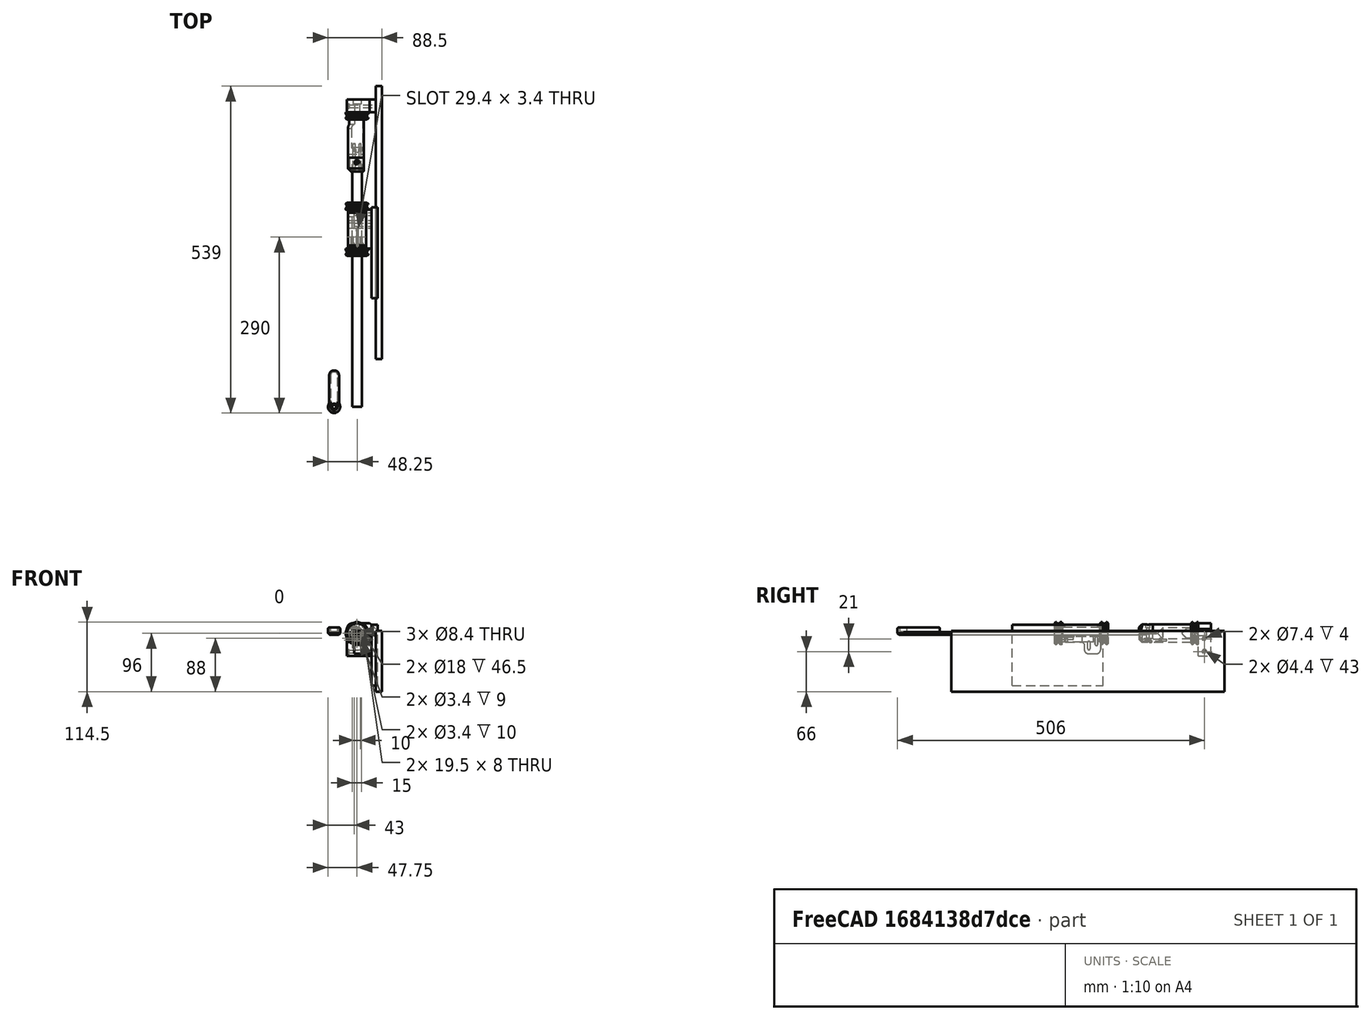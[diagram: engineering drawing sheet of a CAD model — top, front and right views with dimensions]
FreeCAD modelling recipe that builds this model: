
FCSTD DOCUMENT  (FreeCAD 0.16R6703 (Git))
Label: lathe-scale
License: All rights reserved
LicenseURL: http://en.wikipedia.org/wiki/All_rights_reserved
objects: Part::Cylinder×43, Part::Cut×42, Part::Chamfer×35, Part::MultiFuse×35, Part::Box×33, Part::Feature×21, Part::Fillet×11, Part::Mirroring×5, App::DocumentObjectGroup×2, Part::Ellipse×1, Part::Extrusion×1, Part::Fuse×1
note: 228 computed .brp shape members not serialized (recipe doc carries the construction recipe); baked Part::Feature solids carry a one-line shape summary decoded from their .brp

FEATURE [Part::Box] Box  label="scale"
  Height = 4
  Length = 15.5
  Width = 400
FEATURE [Part::Box] Box001  label="slider"
  Height = 15
  Length = 30
  Placement = pos=(-7,263,-2.5) rot=(0,0,1;0rad)
  Width = 60
FEATURE [Part::Ellipse] Ellipse
  Angle0 = 0
  Angle1 = 360
  MajorRadius = 15
  MinorRadius = 10
FEATURE [Part::Feature] Face
  shape: bbox 43.11 x 21.77 x 2e-07 mm, 1 faces, 0 solids (baked)
FEATURE [Part::Extrusion] Extrude
  Base = -> Face
  Dir = (0,0,15)
  Placement = pos=(7.75,390,2) rot=(-1,0,0;1.5708rad)
  Solid = true
  TaperAngle = 15
FEATURE [Part::Cylinder] Cylinder  label="end-cheek"
  Angle = 360
  Height = 3
  Placement = pos=(7.75,486,2) rot=(1,0,0;1.5708rad)
  Radius = 18.5
FEATURE [Part::Cylinder] Cylinder001  label="cable-tie-cyl"
  Angle = 360
  Height = 10
  Placement = pos=(7.75,485,2) rot=(1,0,0;1.5708rad)
  Radius = 16.5
FEATURE [Part::Cylinder] Cylinder002  label="inside-cheek"
  Angle = 360
  Height = 3
  Placement = pos=(7.75,477,2) rot=(1,0,0;1.5708rad)
  Radius = 18.5
FEATURE [Part::Box] Box002  label="lathe-face-1"
  Height = 100
  Length = 10
  Placement = pos=(38.5,79,-94) rot=(0,0,1;0rad)
  Width = 450
FEATURE [Part::Cylinder] Cylinder003
  Angle = 360
  Height = 97
  Placement = pos=(7.75,485,2) rot=(1,0,0;1.5708rad)
  Radius = 15
FEATURE [Part::Chamfer] Chamfer  label="mandrel"
  Base = -> Cylinder003
  Edges = 1 edges r=5: [Edge1]
FEATURE [Part::Box] Box003  label="slot"
  Height = 2
  Length = 35
  Placement = pos=(-10,377,1) rot=(0,0,1;0rad)
  Width = 40
FEATURE [Part::Box] Box004  label="scale-hole"
  Height = 4
  Length = 15.5
  Placement = pos=(0,380,0) rot=(0,0,1;0rad)
  Width = 20
FEATURE [Part::Cylinder] Cylinder004  label="M4"
  Angle = 360
  Height = 36
  Placement = pos=(7.75,403,-15) rot=(0,0,1;0rad)
  Radius = 2.2
FEATURE [Part::Cylinder] Cylinder005  label="M4-head"
  Angle = 360
  Height = 8
  Placement = pos=(7.75,403,11) rot=(0,0,1;0rad)
  Radius = 3.8
FEATURE [Part::Cylinder] Cylinder006
  Angle = 360
  Height = 8
  Placement = pos=(0,0,1) rot=(0,0,1;0rad)
  Radius = 6
FEATURE [Part::Box] Box005  label="Cube"
  Height = 10
  Length = 10
  Placement = pos=(3.7,-5,0) rot=(0,0,1;0rad)
  Width = 10
FEATURE [Part::Feature] Box005001
  Placement = pos=(6.18013,0.704294,0) rot=(0,0,1;1.0472rad)
  shape: bbox 13.66 x 13.66 x 10 mm, 6 faces (baked)
FEATURE [Part::Feature] Box005002
  Placement = pos=(2.48013,5.70429,0) rot=(0,0,1;2.0944rad)
  shape: bbox 13.66 x 13.66 x 10 mm, 6 faces (baked)
FEATURE [Part::Feature] Box005003
  Placement = pos=(-3.7,5,0) rot=(0,0,1;3.14159rad)
  shape: bbox 10 x 10 x 10 mm, 6 faces (baked)
FEATURE [Part::Feature] Box005004
  Placement = pos=(-6.18013,-0.704294,0) rot=(0,0,1;4.18879rad)
  shape: bbox 13.66 x 13.66 x 10 mm, 6 faces (baked)
FEATURE [Part::Feature] Box005005
  Placement = pos=(-2.48013,-5.70429,0) rot=(0,0,-1;1.0472rad)
  shape: bbox 13.66 x 13.66 x 10 mm, 6 faces (baked)
FEATURE [Part::MultiFuse] Fusion
  Shapes = -> [Box005,Box005003,Box005002,Box005004,Box005001,Box005005]
FEATURE [Part::Cut] Cut  label="M4-nut"
  Base = -> Cylinder006
  Placement = pos=(7.75,403,-15) rot=(0,0,1;0rad)
  Tool = -> Fusion
FEATURE [Part::Cylinder] Cylinder007
  Angle = 360
  Height = 70
  Placement = pos=(7.75,485,2) rot=(1,0,0;1.5708rad)
  Radius = 9
FEATURE [Part::Chamfer] Chamfer001  label="hollow"
  Base = -> Cylinder007
  Edges = 1 edges r=8.5: [Edge1]
  Placement = pos=(0,4,0) rot=(0,0,1;0rad)
FEATURE [Part::Box] Box005006  label="gap-expander"
  Height = 30
  Length = 35
  Placement = pos=(19,377,-14) rot=(0,0,1;0rad)
  Width = 140
FEATURE [Part::Cut] Cut001
  Base = -> Chamfer
  Tool = -> Chamfer001
FEATURE [Part::Cut] Cut002
  Base = -> Cut001
  Tool = -> Box005006
FEATURE [Part::Fillet] Fillet
  Base = -> Cut002
  Edges = 1 edges r=4: [Edge4]
FEATURE [Part::Fillet] Fillet001
  Base = -> Fillet
  Edges = 1 edges r=4: [Edge3]
FEATURE [Part::Cut] Cut003
  Base = -> Fillet001
  Tool = -> Box003
FEATURE [Part::Cut] Cut004
  Base = -> Cut003
  Tool = -> Box004
FEATURE [Part::Cut] Cut005
  Base = -> Cut004
  Tool = -> Cut
FEATURE [Part::Cut] Cut006
  Base = -> Cut005
  Tool = -> Cylinder005
FEATURE [Part::Cut] Cut007
  Base = -> Cut006
  Tool = -> Cylinder004
FEATURE [Part::MultiFuse] Fusion001  label="mandrel-no-mount"
  Shapes = -> [Cut007,Cylinder002,Cylinder001,Cylinder]
FEATURE [Part::Box] Box005007  label="bracket-blank"
  Height = 54
  Length = 47.5
  Placement = pos=(-9,486,-35) rot=(0,0,1;0rad)
  Width = 21
FEATURE [Part::Cylinder] Cylinder008
  Angle = 360
  Height = 70
  Placement = pos=(7.75,531,2) rot=(1,0,0;1.5708rad)
  Radius = 4.2
FEATURE [Part::Box] Box005008  label="bracket-blank001"
  Height = 16
  Length = 38
  Placement = pos=(-30,459,-6) rot=(0,0,1;0rad)
  Width = 15
FEATURE [Part::Chamfer] Chamfer002
  Base = -> Box005008
  Edges = 1 edges r=7.5: [Edge10]
FEATURE [Part::Chamfer] Chamfer003  label="nut-access"
  Base = -> Chamfer002
  Edges = 1 edges r=7.5: [Edge8]
FEATURE [Part::Cut] Cut008
  Base = -> Fusion001
  Tool = -> Chamfer003
FEATURE [Part::Chamfer] Chamfer004
  Base = -> Cut008
  Edges = 3 edges r=2: [Edge9,Edge10,Edge11]
FEATURE [Part::Chamfer] Chamfer005
  Base = -> Chamfer004
  Edges = 1 edges r=1.9: [Edge21]
FEATURE [Part::Chamfer] Chamfer006
  Base = -> Chamfer005
  Edges = 1 edges r=1.9: [Edge3]
FEATURE [Part::Cylinder] Cylinder009
  Angle = 360
  Height = 20
  Placement = pos=(7.75,531,2) rot=(1,0,0;1.5708rad)
  Radius = 10
FEATURE [Part::Box] Box005009  label="bracket-blank002"
  Height = 34
  Length = 38
  Placement = pos=(-9,510,8.7) rot=(0,0,1;0rad)
  Width = 22
FEATURE [Part::Feature] Box005009001
  Placement = pos=(5.17737,510,19.8559) rot=(0,1,0;1.0472rad)
  shape: bbox 48.44 x 22 x 49.91 mm, 6 faces (baked)
FEATURE [Part::Feature] Box005009002
  Placement = pos=(21.9274,510,13.1559) rot=(0,1,0;2.0944rad)
  shape: bbox 48.44 x 22 x 49.91 mm, 6 faces (baked)
FEATURE [Part::Feature] Box005009003
  Placement = pos=(24.5,510,-4.7) rot=(0,1,0;3.14159rad)
  shape: bbox 38 x 22 x 34 mm, 6 faces (baked)
FEATURE [Part::Feature] Box005009004
  Placement = pos=(10.3226,510,-15.8559) rot=(0,1,0;4.18879rad)
  shape: bbox 48.44 x 22 x 49.91 mm, 6 faces (baked)
FEATURE [Part::Feature] Box005009005
  Placement = pos=(-6.42737,510,-9.15593) rot=(0,-1,0;1.0472rad)
  shape: bbox 48.44 x 22 x 49.91 mm, 6 faces (baked)
FEATURE [Part::MultiFuse] Fusion002
  Shapes = -> [Box005009,Box005009005,Box005009002,Box005009003,Box005009001,Box005009004]
FEATURE [Part::Cut] Cut009
  Base = -> Cylinder009
  Placement = pos=(0,-51,0) rot=(0,0,1;0rad)
  Tool = -> Fusion002
FEATURE [Part::Cylinder] Cylinder010
  Angle = 360
  Height = 70
  Placement = pos=(7.75,531,2) rot=(1,0,0;1.5708rad)
  Radius = 4.2
FEATURE [Part::MultiFuse] Fusion003  label="M8-hex"
  Shapes = -> [Cylinder008,Cut009]
FEATURE [Part::Cut] Cut010
  Base = -> Chamfer006
  Tool = -> Fusion003
FEATURE [Part::Box] Box005009006  label="bracket-blank003"
  Height = 4
  Length = 17
  Placement = pos=(-9,486.586,-0.8) rot=(1,0,0;0.785398rad)
  Width = 4
FEATURE [Part::Box] Box005009007  label="bracket-blank004"
  Height = 4
  Length = 20
  Placement = pos=(-15,486.2,-0.8) rot=(1,0,0;0.785398rad)
  Width = 4
FEATURE [Part::MultiFuse] Fusion004
  Shapes = -> [Box005007,Box005009006]
FEATURE [Part::Cylinder] Cylinder011
  Angle = 360
  Height = 70
  Placement = pos=(7.75,569,2) rot=(1,0,0;1.5708rad)
  Radius = 6.7
FEATURE [Part::Cut] Cut012
  Base = -> Fusion004
  Tool = -> Cylinder010
FEATURE [Part::Cut] Cut013
  Base = -> Cut012
  Tool = -> Cylinder011
FEATURE [Part::Cylinder] Cylinder012  label="Cylinder"
  Angle = 360
  Height = 50
  Placement = pos=(-12,496,2) rot=(0,1,0;1.5708rad)
  Radius = 2.2
FEATURE [Part::Cylinder] Cylinder013  label="Cylinder012"
  Angle = 360
  Height = 10
  Placement = pos=(-15,496,2) rot=(0,1,0;1.5708rad)
  Radius = 3.7
FEATURE [Part::MultiFuse] Fusion005  label="M4-screw"
  Placement = pos=(0,0,-30) rot=(0,0,1;0rad)
  Shapes = -> [Cylinder012,Cylinder013]
FEATURE [Part::MultiFuse] Fusion006  label="M4-screw001"
  Placement = pos=(0,0,-9) rot=(0,0,1;0rad)
  Shapes = -> [Cylinder012,Cylinder013]
FEATURE [Part::MultiFuse] Fusion007
  Shapes = -> [Fusion005,Fusion006]
FEATURE [Part::Cut] Cut014  label="bracket-a"
  Base = -> Cut013
  Tool = -> Fusion007
FEATURE [Part::Box] Box005009008  label="lathe-face-002"
  Height = 100
  Length = 10
  Placement = pos=(31.5,179,-84) rot=(0,0,1;0rad)
  Width = 150
FEATURE [Part::Cylinder] Cylinder014  label="Cylinder013"
  Angle = 360
  Height = 70
  Radius = 2.2
FEATURE [Part::Cylinder] Cylinder015  label="Cylinder014"
  Angle = 360
  Height = 70
  Placement = pos=(10,0,0) rot=(0,0,1;0rad)
  Radius = 2.2
FEATURE [Part::Box] Box005009009  label="Cube001"
  Height = 70
  Length = 10
  Placement = pos=(0,-2.2,0) rot=(0,0,1;0rad)
  Width = 4.4
FEATURE [Part::MultiFuse] Fusion009  label="M4 slot001"
  Placement = pos=(-26,305.5,-13) rot=(0,1,0;1.5708rad)
  Shapes = -> [Cylinder014,Box005009009,Cylinder015]
FEATURE [Part::Cylinder] Cylinder016  label="inside-cheek001"
  Angle = 360
  Height = 3
  Placement = pos=(7.75,477,2) rot=(1,0,0;1.5708rad)
  Radius = 18.5
FEATURE [Part::Cylinder] Cylinder017  label="cable-tie-cyl001"
  Angle = 360
  Height = 10
  Placement = pos=(7.75,485,2) rot=(1,0,0;1.5708rad)
  Radius = 16.5
FEATURE [Part::Cylinder] Cylinder018  label="end-cheek001"
  Angle = 360
  Height = 3
  Placement = pos=(7.75,486,2) rot=(1,0,0;1.5708rad)
  Radius = 18.5
FEATURE [Part::MultiFuse] Fusion010
  Placement = pos=(0,-149,0) rot=(0,0,1;0rad)
  Shapes = -> [Cylinder016,Cylinder018,Cylinder017]
FEATURE [Part::MultiFuse] Fusion011  label="M4 slot002"
  Placement = pos=(-26,318,-6) rot=(0,1,0;1.5708rad)
  Shapes = -> [Cylinder014,Box005009009,Cylinder015]
FEATURE [Part::Box] Box005009010  label="slider001"
  Height = 29
  Length = 38.5
  Placement = pos=(-7,261,-31.5) rot=(0,0,1;0rad)
  Width = 64
FEATURE [Part::Box] Box005009011  label="slider002"
  Height = 29
  Length = 41
  Placement = pos=(-8,238,-41.5) rot=(0,0,1;0rad)
  Width = 60
FEATURE [Part::Cut] Cut015
  Base = -> Box005009010
  Tool = -> Box005009011
FEATURE [Part::Cylinder] Cylinder019  label="inside-cheek002"
  Angle = 360
  Height = 3
  Placement = pos=(7.75,477,2) rot=(1,0,0;1.5708rad)
  Radius = 18.5
FEATURE [Part::Cylinder] Cylinder020  label="cable-tie-cyl002"
  Angle = 360
  Height = 10
  Placement = pos=(7.75,485,2) rot=(1,0,0;1.5708rad)
  Radius = 16.5
FEATURE [Part::Cylinder] Cylinder021  label="end-cheek002"
  Angle = 360
  Height = 3
  Placement = pos=(7.75,486,2) rot=(1,0,0;1.5708rad)
  Radius = 18.5
FEATURE [Part::MultiFuse] Fusion012
  Placement = pos=(0,-225,0) rot=(0,0,1;0rad)
  Shapes = -> [Cylinder019,Cylinder021,Cylinder020]
FEATURE [Part::Fillet] Fillet002
  Base = -> Cut014
  Edges = 1 edges r=10: [Edge1]
FEATURE [Part::Chamfer] Chamfer007  label="bracket"
  Base = -> Fillet002
  Edges = 1 edges r=10: [Edge3]
FEATURE [App::DocumentObjectGroup] Group  label="Not-printed"
  Group = -> [Box,Box001,Ellipse,Extrude,Box002,Box005009008]
FEATURE [Part::Cylinder] Cylinder022  label="lug"
  Angle = 360
  Height = 6
  Placement = pos=(7.75,328.8,-7) rot=(1,0,0;1.5708rad)
  Radius = 3
FEATURE [Part::Cylinder] Cylinder023  label="lug-hole"
  Angle = 360
  Height = 6
  Placement = pos=(7.75,328,-7) rot=(1,0,0;1.5708rad)
  Radius = 3.1
FEATURE [Part::Chamfer] Chamfer008  label="lug-1"
  Base = -> Cylinder022
  Edges = 1 edges r=2.9: [Edge3]
  Placement = pos=(-6,-1,0) rot=(0,0,1;0rad)
FEATURE [Part::Chamfer] Chamfer009  label="lug-hole-1"
  Base = -> Cylinder023
  Edges = 1 edges r=2.9: [Edge3]
  Placement = pos=(-6,0,0) rot=(0,0,1;0rad)
FEATURE [Part::Chamfer] Chamfer010  label="lug-002"
  Base = -> Cylinder022
  Edges = 1 edges r=2.9: [Edge3]
  Placement = pos=(6,-1,0) rot=(0,0,1;0rad)
FEATURE [Part::Chamfer] Chamfer011  label="lug-hole-002"
  Base = -> Cylinder023
  Edges = 1 edges r=2.9: [Edge3]
  Placement = pos=(6,0,0) rot=(0,0,1;0rad)
FEATURE [Part::Chamfer] Chamfer012  label="lug-003"
  Base = -> Cylinder022
  Edges = 1 edges r=2.9: [Edge3]
  Placement = pos=(-6,-1,0) rot=(0,0,1;0rad)
FEATURE [Part::Chamfer] Chamfer013  label="lug-hole-003"
  Base = -> Cylinder023
  Edges = 1 edges r=2.9: [Edge3]
  Placement = pos=(-6,0,0) rot=(0,0,1;0rad)
FEATURE [Part::Chamfer] Chamfer014  label="lug-004"
  Base = -> Cylinder022
  Edges = 1 edges r=2.9: [Edge3]
  Placement = pos=(6,-1,0) rot=(0,0,1;0rad)
FEATURE [Part::Chamfer] Chamfer015  label="lug-hole-004"
  Base = -> Cylinder023
  Edges = 1 edges r=2.9: [Edge3]
  Placement = pos=(6,0,0) rot=(0,0,1;0rad)
FEATURE [Part::Mirroring] Part__Mirroring  label="lug-003 (Mirror #1)"
  Base = (0,200,0)
  Normal = (0,1,0)
  Source = -> Chamfer012
FEATURE [Part::Mirroring] Part__Mirroring001  label="lug-hole-003 (Mirror #2)"
  Base = (0,200,0)
  Normal = (0,1,0)
  Source = -> Chamfer013
FEATURE [Part::Mirroring] Part__Mirroring002  label="lug-004 (Mirror #3)"
  Base = (0,200,0)
  Normal = (0,1,0)
  Source = -> Chamfer014
FEATURE [Part::Mirroring] Part__Mirroring003  label="lug-hole-004 (Mirror #4)"
  Base = (0,200,0)
  Normal = (0,1,0)
  Source = -> Chamfer015
FEATURE [Part::MultiFuse] Fusion013  label="lug-holes"
  Shapes = -> [Chamfer009,Chamfer011]
FEATURE [Part::MultiFuse] Fusion014  label="lugs"
  Shapes = -> [Chamfer008,Chamfer010]
FEATURE [Part::MultiFuse] Fusion015
  Shapes = -> [Cut015,Fusion014]
FEATURE [Part::Cut] Cut016
  Base = -> Fusion010
  Tool = -> Fusion013
FEATURE [Part::MultiFuse] Fusion016  label="lugs-2"
  Placement = pos=(0,186,0) rot=(0,0,1;0rad)
  Shapes = -> [Part__Mirroring,Part__Mirroring002]
FEATURE [Part::MultiFuse] Fusion017  label="lug-holes-2"
  Placement = pos=(0,186,0) rot=(0,0,1;0rad)
  Shapes = -> [Part__Mirroring001,Part__Mirroring003]
FEATURE [Part::MultiFuse] Fusion018
  Shapes = -> [Fusion015,Fusion016]
FEATURE [Part::Cut] Cut017
  Base = -> Fusion012
  Tool = -> Fusion017
FEATURE [Part::MultiFuse] Fusion019
  Shapes = -> [Fusion011,Fusion009]
FEATURE [Part::Cut] Cut018
  Base = -> Fusion018
  Tool = -> Fusion019
FEATURE [Part::Box] Box005009012  label="scale-hole001"
  Height = 8
  Length = 19.5
  Placement = pos=(-2,0,-2) rot=(0,0,1;0rad)
  Width = 400
FEATURE [Part::Box] Box005009013  label="scale-hole002"
  Height = 8
  Length = 19.5
  Placement = pos=(-2,0,-2) rot=(0,0,1;0rad)
  Width = 400
FEATURE [Part::Cut] Cut019
  Base = -> Cut016
  Tool = -> Box005009012
FEATURE [Part::Cut] Cut020
  Base = -> Cut017
  Tool = -> Box005009013
FEATURE [Part::Cut] Cut021  label="completed-mandrel001"
  Base = -> Cut010
  Tool = -> Box005009007
FEATURE [Part::Box] Box005009014  label="slider003"
  Height = 5
  Length = 30
  Placement = pos=(-7,261,13) rot=(0,0,1;0rad)
  Width = 5
FEATURE [Part::Chamfer] Chamfer016
  Base = -> Box005009014
  Edges = 1 edges r=4: [Edge2]
FEATURE [Part::Chamfer] Chamfer017
  Base = -> Chamfer016
  Edges = 1 edges r=4: [Edge15]
FEATURE [Part::Chamfer] Chamfer018
  Base = -> Chamfer017
  Edges = 1 edges r=3.9: [Edge7]
FEATURE [Part::Chamfer] Chamfer019
  Base = -> Chamfer017
  Edges = 1 edges r=3.9: [Edge7]
FEATURE [Part::MultiFuse] Fusion020
  Shapes = -> [Chamfer018,Cut020]
FEATURE [Part::Mirroring] Part__Mirroring005  label="Chamfer019 (Mirror #6)"
  Base = (0,250,0)
  Normal = (0,1,0)
  Placement = pos=(0,86,0) rot=(0,0,1;0rad)
  Source = -> Chamfer019
FEATURE [Part::Chamfer] Chamfer020
  Base = -> Fusion020
  Edges = 1 edges r=1.9: [Edge52]
FEATURE [Part::Chamfer] Chamfer021
  Base = -> Chamfer020
  Edges = 1 edges r=1.9: [Edge14]
FEATURE [Part::Chamfer] Chamfer022  label="slider-end-r-a"
  Base = -> Chamfer021
  Edges = 1 edges r=1.9: [Edge22]
FEATURE [Part::MultiFuse] Fusion021
  Shapes = -> [Cut019,Part__Mirroring005]
FEATURE [Part::Chamfer] Chamfer023
  Base = -> Fusion021
  Edges = 1 edges r=1.9: [Edge2]
FEATURE [Part::Chamfer] Chamfer024
  Base = -> Chamfer023
  Edges = 1 edges r=1.9: [Edge57]
FEATURE [Part::Chamfer] Chamfer025  label="slider-end-l"
  Base = -> Chamfer024
  Edges = 1 edges r=1.9: [Edge6]
FEATURE [Part::Cylinder] Cylinder024  label="Cylinder015"
  Angle = 360
  Height = 20
  Placement = pos=(8.25,267,-17) rot=(0,0,1;0rad)
  Radius = 1.7
FEATURE [Part::Box] Box005009015  label="Cube002"
  Height = 20
  Length = 3.4
  Placement = pos=(6.55,267,-17) rot=(0,0,1;0rad)
  Width = 26
FEATURE [Part::Cylinder] Cylinder025  label="Cylinder016"
  Angle = 360
  Height = 20
  Placement = pos=(8.25,293,-17) rot=(0,0,1;0rad)
  Radius = 1.7
FEATURE [Part::MultiFuse] Fusion022  label="slider-screw-slot"
  Shapes = -> [Cylinder024,Cylinder025,Box005009015]
FEATURE [Part::Cut] Cut022
  Base = -> Cut018
  Tool = -> Fusion022
FEATURE [Part::Chamfer] Chamfer026
  Base = -> Cut022
  Edges = 1 edges r=3: [Edge22]
FEATURE [Part::Fillet] Fillet003
  Base = -> Chamfer026
  Edges = 1 edges r=7: [Edge31]
FEATURE [Part::Fillet] Fillet004  label="slider-support-a"
  Base = -> Fillet003
  Edges = 1 edges r=7: [Edge26]
FEATURE [Part::Cylinder] Cylinder026  label="Cylinder017"
  Angle = 360
  Height = 30
  Placement = pos=(0,0,1) rot=(0,0,1;0rad)
  Radius = 1.7
FEATURE [Part::Cylinder] Cylinder027  label="Cylinder018"
  Angle = 360
  Height = 4
  Radius = 3
FEATURE [Part::Box] Box005009016  label="Cube003"
  Height = 3
  Length = 16
  Placement = pos=(-3.2,-2.8,18) rot=(0,0,1;0rad)
  Width = 5.6
FEATURE [Part::MultiFuse] Fusion023  label="M3-cavity"
  Placement = pos=(0,249,-6) rot=(-0.57735,0.57735,0.57735;2.0944rad)
  Shapes = -> [Cylinder026,Cylinder027,Box005009016]
FEATURE [Part::MultiFuse] Fusion024  label="M3-cavity001"
  Placement = pos=(15,249,-6) rot=(-0.57735,0.57735,0.57735;2.0944rad)
  Shapes = -> [Cylinder026,Cylinder027,Box005009016]
FEATURE [Part::MultiFuse] Fusion025  label="M3-cavity002"
  Placement = pos=(0,249,-6) rot=(-0.57735,0.57735,0.57735;2.0944rad)
  Shapes = -> [Cylinder026,Cylinder027,Box005009016]
FEATURE [Part::MultiFuse] Fusion026  label="M3-cavity003"
  Placement = pos=(15,249,-6) rot=(-0.57735,0.57735,0.57735;2.0944rad)
  Shapes = -> [Cylinder026,Cylinder027,Box005009016]
FEATURE [Part::Cut] Cut023
  Base = -> Fillet004
  Tool = -> Fusion023
FEATURE [Part::Cut] Cut024  label="slider-support-a001"
  Base = -> Cut023
  Tool = -> Fusion024
FEATURE [Part::Cut] Cut025
  Base = -> Chamfer022
  Tool = -> Fusion025
FEATURE [Part::Cut] Cut026  label="slide-end-r"
  Base = -> Cut025
  Tool = -> Fusion026
FEATURE [Part::Box] Box005009017  label="Cube004"
  Height = 26
  Length = 20
  Placement = pos=(-17,294,-38) rot=(0,0,1;0rad)
  Width = 33
FEATURE [Part::Box] Box005009018  label="Cube005"
  Height = 26
  Length = 20
  Placement = pos=(-17,313,-27) rot=(0,0,1;0rad)
  Width = 10
FEATURE [Part::Fuse] Fusion027
  Base = -> Box005009017
  Tool = -> Box005009018
FEATURE [Part::Cut] Cut027  label="slider-support"
  Base = -> Cut024
  Tool = -> Fusion027
FEATURE [Part::Cylinder] Cylinder028  label="Cylinder019"
  Angle = 360
  Height = 12
  Radius = 10
FEATURE [Part::Cylinder] Cylinder029  label="Cylinder020"
  Angle = 360
  Height = 20
  Placement = pos=(0,0,-4) rot=(0,0,1;0rad)
  Radius = 3.2
FEATURE [Part::Cylinder] Cylinder030  label="Cylinder021"
  Angle = 360
  Height = 12
  Placement = pos=(0,0,5) rot=(0,0,1;0rad)
  Radius = 5.5
FEATURE [Part::MultiFuse] Fusion028  label="M6"
  Shapes = -> [Cylinder029,Cylinder030]
FEATURE [Part::Box] Box005009019  label="Cube006"
  Height = 12
  Length = 16
  Placement = pos=(-8,0,0) rot=(0,0,1;0rad)
  Width = 60
FEATURE [Part::MultiFuse] Fusion029
  Shapes = -> [Box005009019,Cylinder028]
FEATURE [Part::Fillet] Fillet005
  Base = -> Fusion029
  Edges = 1 edges r=20: [Edge12]
FEATURE [Part::Fillet] Fillet006
  Base = -> Fillet005
  Edges = 1 edges r=20: [Edge18]
FEATURE [Part::Fillet] Fillet007
  Base = -> Fillet006
  Edges = 2 edges r=7: [Edge9,Edge18]
FEATURE [Part::Fillet] Fillet008
  Base = -> Fillet007
  Edges = 9 edges r=2.5: [Edge9,Edge13,Edge22,Edge24,Edge25,Edge31,Edge32,Edge35,Edge36]
FEATURE [Part::Chamfer] Chamfer027
  Base = -> Fillet008
  Edges = 9 edges r=2.5: [Edge3,Edge6,Edge12,Edge14,Edge16,Edge18,Edge32,Edge33,Edge34]
FEATURE [Part::Cut] Cut028  label="lead-screw-handle"
  Base = -> Chamfer027
  Placement = pos=(-30,0,0) rot=(0,0,1;0rad)
  Tool = -> Fusion028
FEATURE [Part::Cylinder] Cylinder031  label="end-cheek003"
  Angle = 360
  Height = 3
  Placement = pos=(7.75,486,2) rot=(1,0,0;1.5708rad)
  Radius = 18.5
FEATURE [Part::Cylinder] Cylinder032  label="cable-tie-cyl003"
  Angle = 360
  Height = 10
  Placement = pos=(7.75,485,2) rot=(1,0,0;1.5708rad)
  Radius = 16.5
FEATURE [Part::Cylinder] Cylinder033  label="inside-cheek003"
  Angle = 360
  Height = 3
  Placement = pos=(7.75,477,2) rot=(1,0,0;1.5708rad)
  Radius = 18.5
FEATURE [Part::Cylinder] Cylinder034
  Angle = 360
  Height = 97
  Placement = pos=(7.75,485,2) rot=(1,0,0;1.5708rad)
  Radius = 15
FEATURE [Part::Chamfer] Chamfer028  label="mandrel001"
  Base = -> Cylinder034
  Edges = 1 edges r=5: [Edge1]
FEATURE [Part::Box] Box005009020  label="slot001xxx"
  Height = 2
  Length = 35
  Placement = pos=(-10,332,1) rot=(0,0,1;0rad)
  Width = 40
FEATURE [Part::Box] Box005009021  label="scale-hole003"
  Height = 4
  Length = 15.5
  Placement = pos=(0,380,0) rot=(0,0,1;0rad)
  Width = 20
FEATURE [Part::Cylinder] Cylinder035  label="M007"
  Angle = 360
  Height = 36
  Placement = pos=(7.75,405,-15) rot=(0,0,1;0rad)
  Radius = 2.2
FEATURE [Part::Cylinder] Cylinder036  label="M4-head001"
  Angle = 360
  Height = 8
  Placement = pos=(7.75,405,11) rot=(0,0,1;0rad)
  Radius = 3.8
FEATURE [Part::Cylinder] Cylinder037
  Angle = 360
  Height = 8
  Placement = pos=(0,0,1) rot=(0,0,1;0rad)
  Radius = 6
FEATURE [Part::Box] Box005009022  label="Cube007"
  Height = 10
  Length = 10
  Placement = pos=(3.7,-5,0) rot=(0,0,1;0rad)
  Width = 10
FEATURE [Part::Feature] Box005009023
  Placement = pos=(6.18013,0.704294,0) rot=(0,0,1;1.0472rad)
  shape: bbox 13.66 x 13.66 x 10 mm, 6 faces (baked)
FEATURE [Part::Feature] Box005009024
  Placement = pos=(2.48013,5.70429,0) rot=(0,0,1;2.0944rad)
  shape: bbox 13.66 x 13.66 x 10 mm, 6 faces (baked)
FEATURE [Part::Feature] Box005009025
  Placement = pos=(-3.7,5,0) rot=(0,0,1;3.14159rad)
  shape: bbox 10 x 10 x 10 mm, 6 faces (baked)
FEATURE [Part::Feature] Box005009026
  Placement = pos=(-6.18013,-0.704294,0) rot=(0,0,1;4.18879rad)
  shape: bbox 13.66 x 13.66 x 10 mm, 6 faces (baked)
FEATURE [Part::Feature] Box005009027
  Placement = pos=(-2.48013,-5.70429,0) rot=(0,0,-1;1.0472rad)
  shape: bbox 13.66 x 13.66 x 10 mm, 6 faces (baked)
FEATURE [Part::MultiFuse] Fusion030
  Shapes = -> [Box005009022,Box005009025,Box005009024,Box005009026,Box005009023,Box005009027]
FEATURE [Part::Cut] Cut029  label="M4-nut001"
  Base = -> Cylinder037
  Placement = pos=(7.75,405,-19) rot=(0,0,1;0rad)
  Tool = -> Fusion030
FEATURE [Part::Cylinder] Cylinder038
  Angle = 360
  Height = 70
  Placement = pos=(7.75,485,2) rot=(1,0,0;1.5708rad)
  Radius = 9
FEATURE [Part::Chamfer] Chamfer029  label="hollow001"
  Base = -> Cylinder038
  Edges = 1 edges r=8.5: [Edge1]
  Placement = pos=(0,4,0) rot=(0,0,1;0rad)
FEATURE [Part::Box] Box005009028  label="gap-expander001"
  Height = 30
  Length = 35
  Placement = pos=(19,377,-14) rot=(0,0,1;0rad)
  Width = 140
FEATURE [Part::Cut] Cut030
  Base = -> Chamfer028
  Tool = -> Chamfer029
FEATURE [Part::Cut] Cut031
  Base = -> Cut030
  Tool = -> Box005009028
FEATURE [Part::Fillet] Fillet009
  Base = -> Cut031
  Edges = 1 edges r=4: [Edge4]
FEATURE [Part::Fillet] Fillet010
  Base = -> Fillet009
  Edges = 1 edges r=4: [Edge3]
FEATURE [Part::Cut] Cut032
  Base = -> Fillet010
  Tool = -> Box005009020
FEATURE [Part::Cut] Cut033
  Base = -> Cut032
  Tool = -> Box005009021
FEATURE [Part::Cut] Cut034
  Base = -> Cut033
  Tool = -> Cut029
FEATURE [Part::Cut] Cut035
  Base = -> Cut034
  Tool = -> Cylinder036
FEATURE [Part::Cut] Cut036
  Base = -> Cut035
  Tool = -> Cylinder035
FEATURE [Part::MultiFuse] Fusion031  label="mandrel-no-mount001"
  Shapes = -> [Cut036,Cylinder033,Cylinder032,Cylinder031]
FEATURE [Part::Cylinder] Cylinder039
  Angle = 360
  Height = 70
  Placement = pos=(7.75,531,2) rot=(1,0,0;1.5708rad)
  Radius = 4.2
FEATURE [Part::Box] Box005009029  label="bracket-blank005"
  Height = 16
  Length = 38
  Placement = pos=(-30,459,-6) rot=(0,0,1;0rad)
  Width = 15
FEATURE [Part::Chamfer] Chamfer030
  Base = -> Box005009029
  Edges = 1 edges r=7.5: [Edge10]
FEATURE [Part::Chamfer] Chamfer031  label="nut-access001"
  Base = -> Chamfer030
  Edges = 1 edges r=7.5: [Edge8]
FEATURE [Part::Cut] Cut037
  Base = -> Fusion031
  Tool = -> Chamfer031
FEATURE [Part::Chamfer] Chamfer032
  Base = -> Cut037
  Edges = 3 edges r=2: [Edge9,Edge10,Edge11]
FEATURE [Part::Chamfer] Chamfer033
  Base = -> Chamfer032
  Edges = 1 edges r=1.9: [Edge21]
FEATURE [Part::Chamfer] Chamfer034
  Base = -> Chamfer033
  Edges = 1 edges r=1.9: [Edge3]
FEATURE [Part::Cylinder] Cylinder040
  Angle = 360
  Height = 20
  Placement = pos=(7.75,531,2) rot=(1,0,0;1.5708rad)
  Radius = 10
FEATURE [Part::Box] Box005009030  label="bracket-blank006"
  Height = 34
  Length = 38
  Placement = pos=(-9,510,8.7) rot=(0,0,1;0rad)
  Width = 22
FEATURE [Part::Feature] Box005009031
  Placement = pos=(5.17737,510,19.8559) rot=(0,1,0;1.0472rad)
  shape: bbox 48.44 x 22 x 49.91 mm, 6 faces (baked)
FEATURE [Part::Feature] Box005009032
  Placement = pos=(21.9274,510,13.1559) rot=(0,1,0;2.0944rad)
  shape: bbox 48.44 x 22 x 49.91 mm, 6 faces (baked)
FEATURE [Part::Feature] Box005009033
  Placement = pos=(24.5,510,-4.7) rot=(0,1,0;3.14159rad)
  shape: bbox 38 x 22 x 34 mm, 6 faces (baked)
FEATURE [Part::Feature] Box005009034
  Placement = pos=(10.3226,510,-15.8559) rot=(0,1,0;4.18879rad)
  shape: bbox 48.44 x 22 x 49.91 mm, 6 faces (baked)
FEATURE [Part::Feature] Box005009035
  Placement = pos=(-6.42737,510,-9.15593) rot=(0,-1,0;1.0472rad)
  shape: bbox 48.44 x 22 x 49.91 mm, 6 faces (baked)
FEATURE [Part::MultiFuse] Fusion032
  Shapes = -> [Box005009030,Box005009035,Box005009032,Box005009033,Box005009031,Box005009034]
FEATURE [Part::Cut] Cut038
  Base = -> Cylinder040
  Placement = pos=(0,-51,0) rot=(0,0,1;0rad)
  Tool = -> Fusion032
FEATURE [Part::MultiFuse] Fusion033  label="M8-hex001"
  Shapes = -> [Cylinder039,Cut038]
FEATURE [Part::Cut] Cut039
  Base = -> Chamfer034
  Tool = -> Fusion033
FEATURE [Part::Box] Box005009036  label="bracket-blank007"
  Height = 4
  Length = 20
  Placement = pos=(-15,486.2,-0.8) rot=(1,0,0;0.785398rad)
  Width = 4
FEATURE [Part::Cut] Cut040  label="completed-mandrel002"
  Base = -> Cut039
  Tool = -> Box005009036
FEATURE [Part::Box] Box005009037  label="Cube008"
  Height = 29
  Length = 40
  Placement = pos=(-13,387,-6.3) rot=(0,0,1;0rad)
  Width = 24
FEATURE [Part::Cut] Cut041
  Base = -> Cut040
  Tool = -> Box005009037
FEATURE [Part::Cylinder] Cylinder041  label="Cylinder043"
  Angle = 360
  Height = 50
  Placement = pos=(0,0,1) rot=(0,0,1;0rad)
  Radius = 1.7
FEATURE [Part::Cylinder] Cylinder042  label="Cylinder044"
  Angle = 360
  Height = 4
  Radius = 3
FEATURE [Part::Box] Box005009038  label="Cube009"
  Height = 3
  Length = 16
  Placement = pos=(-3.2,-2.8,39) rot=(0,0,1;0rad)
  Width = 5.6
FEATURE [Part::MultiFuse] Fusion034  label="M3-cavity004"
  Placement = pos=(13,383,-9) rot=(-0.57735,0.57735,0.57735;2.0944rad)
  Shapes = -> [Cylinder041,Cylinder042,Box005009038]
FEATURE [Part::MultiFuse] Fusion035  label="M3-cavity005"
  Placement = pos=(3,383,-9) rot=(-0.57735,0.57735,0.57735;2.0944rad)
  Shapes = -> [Cylinder041,Cylinder042,Box005009038]
FEATURE [Part::MultiFuse] Fusion036
  Shapes = -> [Fusion034,Fusion035]
FEATURE [Part::Cut] Cut042  label="mandrel-metal-clamp"
  Base = -> Cut041
  Tool = -> Fusion036
FEATURE [App::DocumentObjectGroup] Group001  label="Finished-parts"
  Group = -> [Chamfer007,Cut021,Chamfer025,Cut026,Cut027,Cut028,Cut042]
